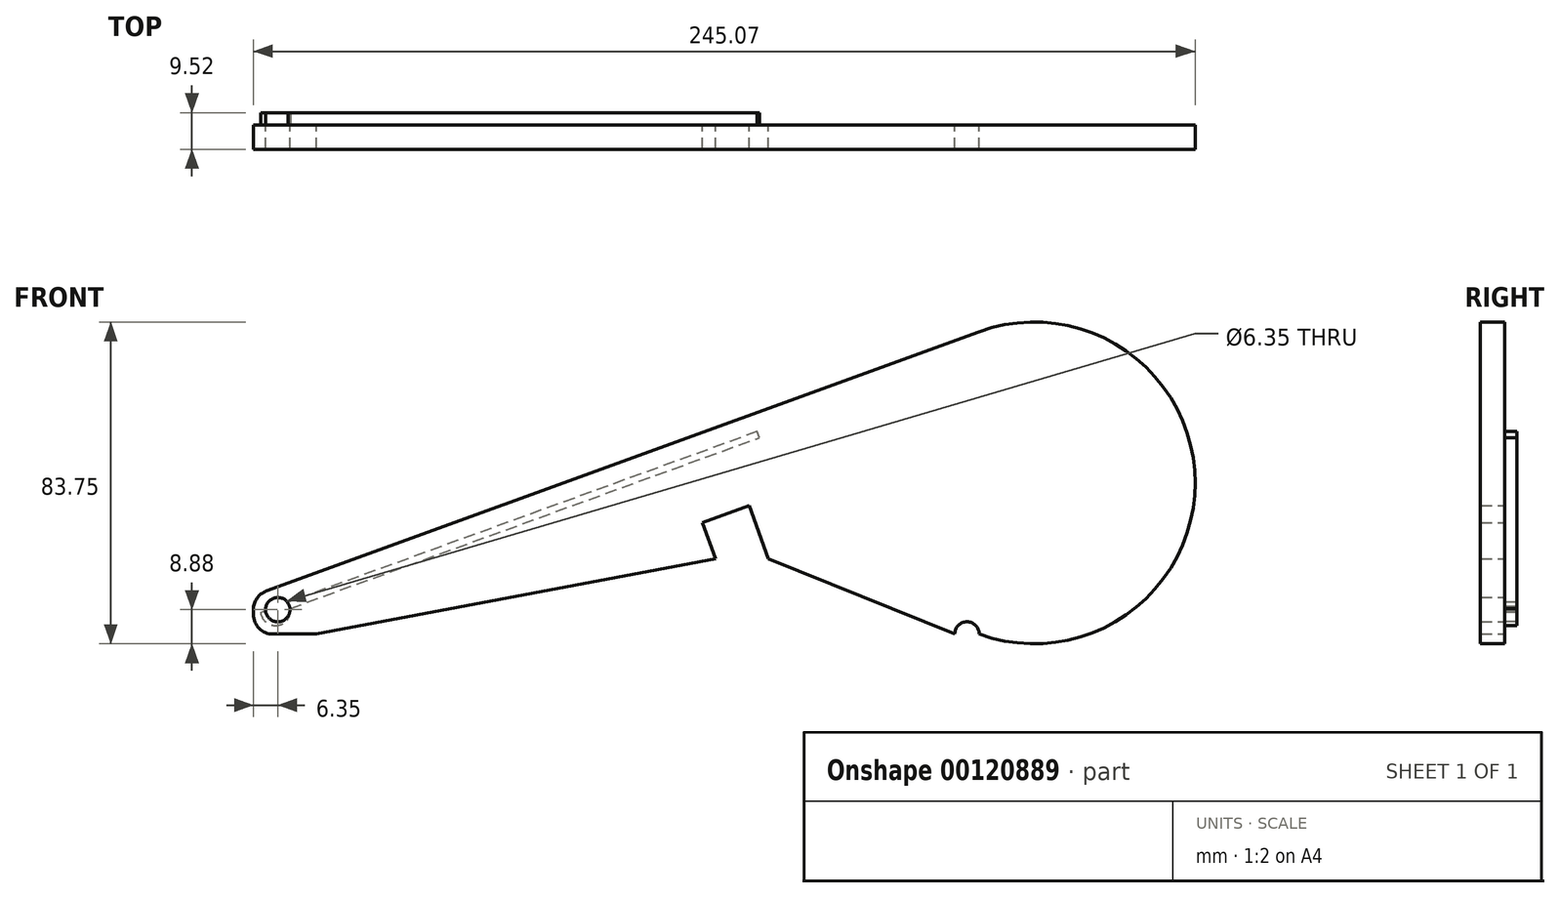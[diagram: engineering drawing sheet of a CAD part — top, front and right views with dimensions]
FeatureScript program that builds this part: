
annotation { "Feature Type Name" : "Feature", "Feature Type Description" : "" }
export const myFeature = defineFeature(function(context is Context, id is Id, definition is map)
    precondition{}
    {
        {
            var Q0;
            Q0=qCreatedBy(makeId("Front.planeOp"),FACE);
            var sketch = newSketch(context, id + "F0", { "sketchPlane" : qUnion([Q0])});
            skLineSegment(sketch, "E0", {"start": v(0, 0) * mm, "end": v(0, 9.95) * mm});
            skLineSegment(sketch, "E1", {"start": v(0, 9.95) * mm, "end": v(188.88, 78.7) * mm});
            skArc(sketch, "E2", {"start": v(188.88, 0) * mm, "mid": v(245.07, 39.35) * mm, "end": v(188.88, 78.7) * mm});
            skLineSegment(sketch, "E3", {"start": v(0, 0) * mm, "end": v(16.42, 0) * mm});
            skLineSegment(sketch, "E4", {"start": v(16.42, 0) * mm, "end": v(120.29, 19.62) * mm});
            skLineSegment(sketch, "E5", {"start": v(116.88, 28.98) * mm, "end": v(129.01, 33.4) * mm});
            skLineSegment(sketch, "E6", {"start": v(129.01, 33.4) * mm, "end": v(134.03, 19.62) * mm});
            skLineSegment(sketch, "E7", {"start": v(134.03, 19.62) * mm, "end": v(182.53, 0) * mm});
            skArc(sketch, "E8", {"start": v(188.88, 0) * mm, "mid": v(185.7, 3.18) * mm, "end": v(182.53, 0) * mm});
            skLineSegment(sketch, "E9", {"start": v(120.29, 19.62) * mm, "end": v(116.88, 28.98) * mm});
            skCircle(sketch, "E10", {"center": v(6.35, 6.35) * mm, "radius": 3.17 * mm});
            skSolve(sketch);
        }
        {
            var Q0;
            Q0=makeQuery(id+"F0.imprint","IMPRINT",FACE,{"disambiguationData":[TD([[makeQuery(id+"F0.imprint","IMPRINT",EDGE,{"derivedFrom":sQuery(id+"F0.wireOp",EDGE,"E0")}),-1.0]])]});
            extrude(context, id + "F1", {"entities" : qUnion([Q0]), "depth" : 6.35 * mm});
        }
        {
            var Q0;
            Q0=makeQuery(id+"F1.opExtrude","SWEPT_EDGE",EDGE,{"disambiguationData":[OSD([sQuery(id+"F0.wireOp",EDGE,"E0"),sQuery(id+"F0.wireOp",EDGE,"E1")])]});
            var Q1;
            Q1=makeQuery(id+"F1.opExtrude","SWEPT_EDGE",EDGE,{"disambiguationData":[OSD([sQuery(id+"F0.wireOp",EDGE,"E0"),sQuery(id+"F0.wireOp",EDGE,"E3")])]});
            fillet(context, id + "F2", {"entities" : qUnion([Q0, Q1]), "radius" : 5.08 * mm, "tangentPropagation" : true, "allowEdgeOverflow" : false});
        }
        {
            var Q0;
            Q0=makeQuery(id+"F1.opExtrude","CAP_FACE",FACE,{"disambiguationData":[OSD([sQuery(id+"F0.wireOp",EDGE,"E0"),sQuery(id+"F0.wireOp",EDGE,"E1"),sQuery(id+"F0.wireOp",EDGE,"E2"),sQuery(id+"F0.wireOp",EDGE,"E3"),sQuery(id+"F0.wireOp",EDGE,"E4"),sQuery(id+"F0.wireOp",EDGE,"E5"),sQuery(id+"F0.wireOp",EDGE,"E6"),sQuery(id+"F0.wireOp",EDGE,"E7"),sQuery(id+"F0.wireOp",EDGE,"E8"),sQuery(id+"F0.wireOp",EDGE,"E9"),sQuery(id+"F0.wireOp",EDGE,"E10")])],"isStart":true});
            var sketch = newSketch(context, id + "F3", { "sketchPlane" : qUnion([Q0])});
            skLineSegment(sketch, "E11", {"start": v(-131.07, 52.7) * mm, "end": v(-9.03, 8.28) * mm});
            skLineSegment(sketch, "E12", {"start": v(-9.03, 8.28) * mm, "end": v(-9.6, 6.7) * mm});
            skLineSegment(sketch, "E13", {"start": v(-9.6, 6.7) * mm, "end": v(-131.64, 51.1) * mm});
            skLineSegment(sketch, "E14", {"start": v(-131.64, 51.1) * mm, "end": v(-131.07, 52.7) * mm});
            skSolve(sketch);
        }
        {
            var Q0;
            Q0=makeQuery(id+"F3.imprint","IMPRINT",FACE,{"disambiguationData":[TD([[makeQuery(id+"F3.imprint","IMPRINT",EDGE,{"derivedFrom":sQuery(id+"F3.wireOp",EDGE,"E11")}),-1.0]])]});
            extrude(context, id + "F4", {"entities" : qUnion([Q0]), "operationType" : NewBodyOperationType.ADD, "depth" : 3.17 * mm});
        }
        {
            var Q0;
            Q0=makeQuery(id+"F1.opExtrude","CAP_FACE",FACE,{"disambiguationData":[OSD([sQuery(id+"F0.wireOp",EDGE,"E0"),sQuery(id+"F0.wireOp",EDGE,"E1"),sQuery(id+"F0.wireOp",EDGE,"E2"),sQuery(id+"F0.wireOp",EDGE,"E3"),sQuery(id+"F0.wireOp",EDGE,"E4"),sQuery(id+"F0.wireOp",EDGE,"E5"),sQuery(id+"F0.wireOp",EDGE,"E6"),sQuery(id+"F0.wireOp",EDGE,"E7"),sQuery(id+"F0.wireOp",EDGE,"E8"),sQuery(id+"F0.wireOp",EDGE,"E9"),sQuery(id+"F0.wireOp",EDGE,"E10")])],"isStart":true});
            var sketch = newSketch(context, id + "F5", { "sketchPlane" : qUnion([Q0])});
            skArc(sketch, "E15", {"start": v(-9.6, 6.7) * mm, "mid": v(-6.26, 2.23) * mm, "end": v(-1.89, 5.68) * mm});
            skCircle(sketch, "E16", {"center": v(-6.35, 6.35) * mm, "radius": 3.19 * mm});
            skLineSegment(sketch, "E17", {"start": v(-9.03, 8.28) * mm, "end": v(-1.89, 5.68) * mm, "construction": true});
            skLineSegment(sketch, "E18", {"start": v(-1.89, 5.68) * mm, "end": v(-3.18, 6.15) * mm});
            skSolve(sketch);
        }
        {
            var Q0;
            {var subQ0=sQuery(id+"F5.wireOp",EDGE,"E15");Q0=makeQuery(id+"F5.imprint","IMPRINT",FACE,{"disambiguationData":[TD([[makeQuery(id+"F5.imprint","IMPRINT",EDGE,{"derivedFrom":subQ0}),1.0]])]});}
            extrude(context, id + "F6", {"entities" : qUnion([Q0]), "operationType" : NewBodyOperationType.ADD, "depth" : 3.17 * mm});
        }
    });
